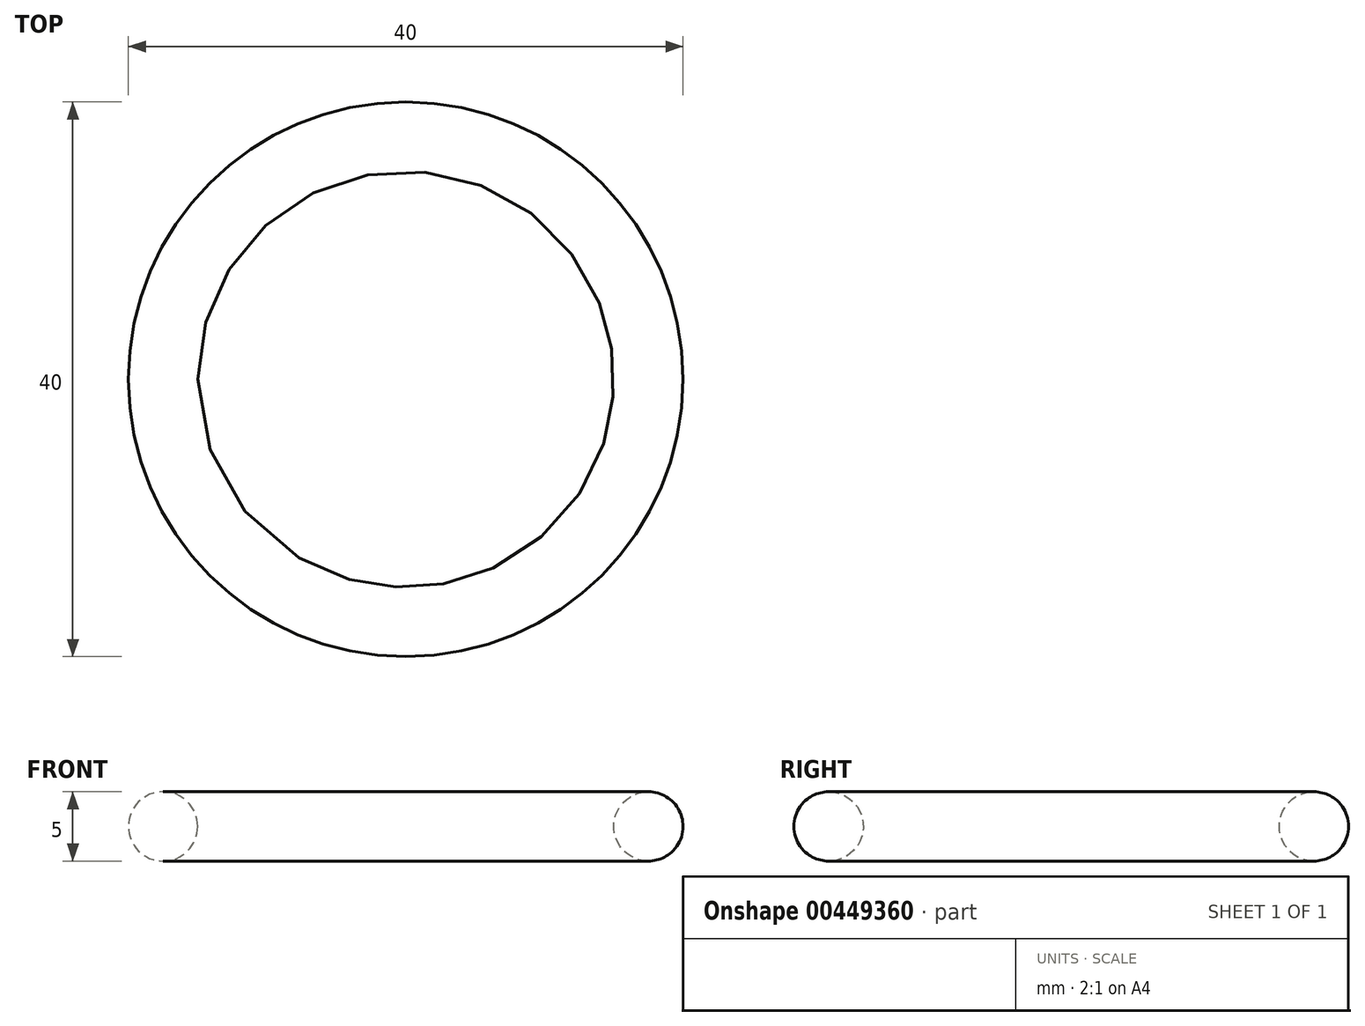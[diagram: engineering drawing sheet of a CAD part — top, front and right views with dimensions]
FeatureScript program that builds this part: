
annotation { "Feature Type Name" : "Feature", "Feature Type Description" : "" }
export const myFeature = defineFeature(function(context is Context, id is Id, definition is map)
    precondition{}
    {
        {
            var Q0;
            Q0=qCreatedBy(makeId("Front.planeOp"),FACE);
            var sketch = newSketch(context, id + "F0", { "sketchPlane" : qUnion([Q0])});
            skLineSegment(sketch, "E0", {"start": v(0, 0) * mm, "end": v(0, 1.64) * mm, "construction": true});
            skCircle(sketch, "E1", {"center": v(17.5, 0) * mm, "radius": 2.5 * mm});
            skSolve(sketch);
        }
        {
            var Q0;
            Q0=makeQuery(id+"F0.imprint","IMPRINT",FACE,{"disambiguationData":[TD([[makeQuery(id+"F0.imprint","IMPRINT",EDGE,{"derivedFrom":sQuery(id+"F0.wireOp",EDGE,"E1")}),1.0]])]});
            var Q1;
            Q1=sQuery(id+"F0.wireOp",EDGE,"E0");
            revolve(context, id + "F1", {"entities" : qUnion([Q0]), "axis" : qUnion([Q1]), "revolveType" : RevolveType.FULL});
        }
    });
